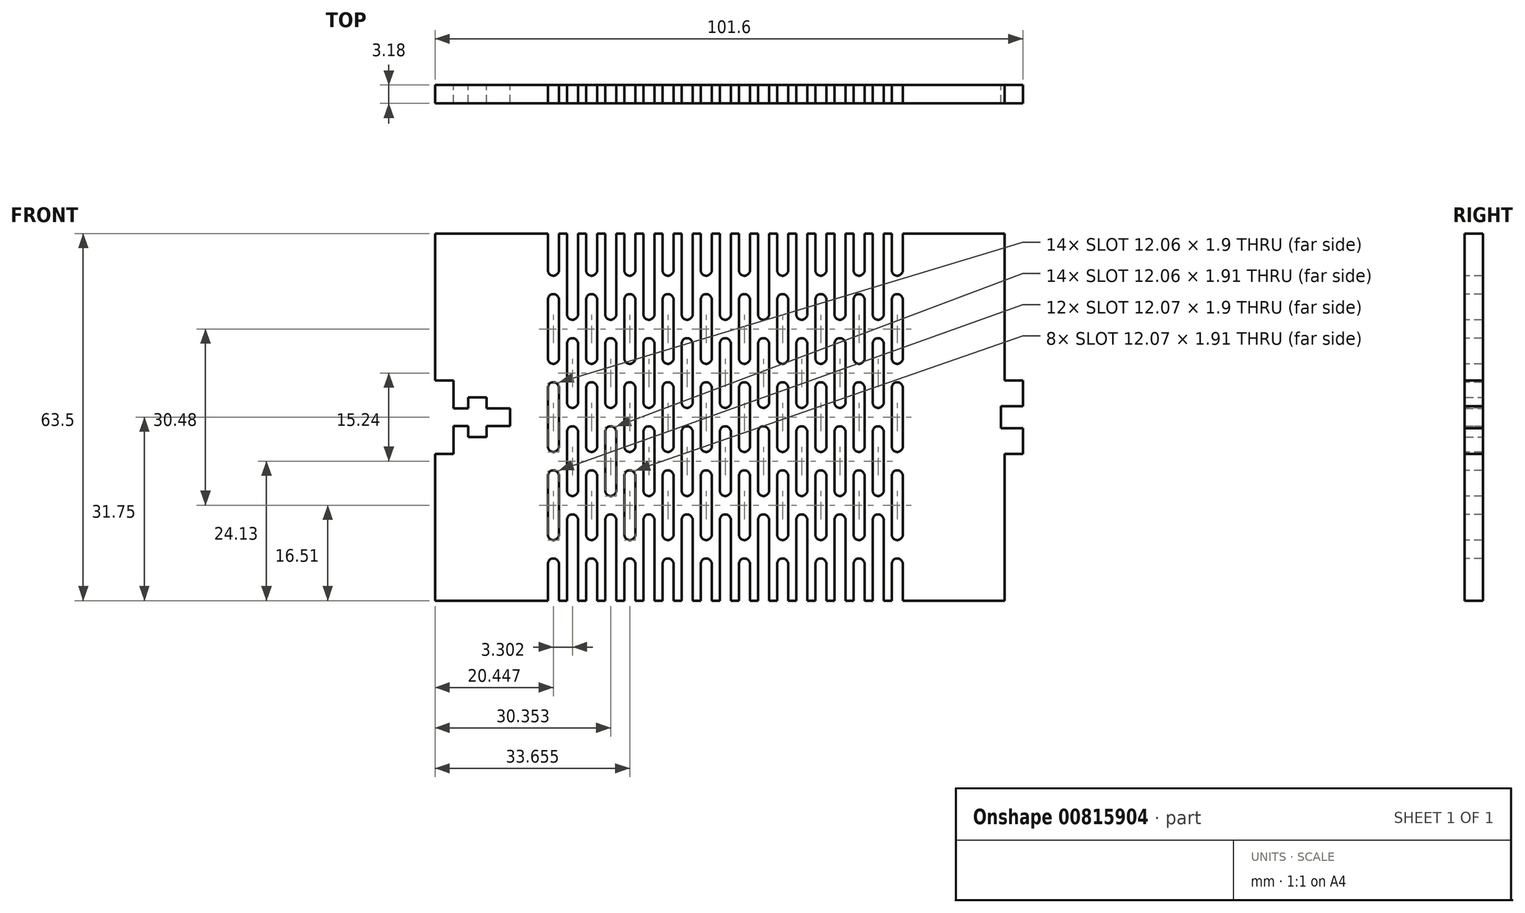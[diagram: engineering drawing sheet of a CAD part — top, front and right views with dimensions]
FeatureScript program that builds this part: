
annotation { "Feature Type Name" : "Feature", "Feature Type Description" : "" }
export const myFeature = defineFeature(function(context is Context, id is Id, definition is map)
    precondition{}
    {
        {
            var Q0;
            Q0=qCreatedBy(makeId("Front.planeOp"),FACE);
            var sketch = newSketch(context, id + "F0", { "sketchPlane" : qUnion([Q0])});
            skLineSegment(sketch, "E0.bottom", {"start": v(50.8, 31.75) * mm, "end": v(-50.8, 31.75) * mm});
            skLineSegment(sketch, "E0.top", {"start": v(50.8, -31.75) * mm, "end": v(-50.8, -31.75) * mm});
            skLineSegment(sketch, "E0.left", {"start": v(50.8, 31.75) * mm, "end": v(50.8, -31.75) * mm});
            skLineSegment(sketch, "E0.right", {"start": v(-50.8, 31.75) * mm, "end": v(-50.8, -31.75) * mm});
            skPoint(sketch, "E0.middle", {"position": v(0, 0) * mm});
            skLineSegment(sketch, "E1", {"start": v(-50.8, 0) * mm, "end": v(50.8, 0) * mm, "construction": true});
            skSolve(sketch);
        }
        {
            var Q0;
            Q0=makeQuery(id+"F0.imprint","IMPRINT",FACE,{"disambiguationData":[TD([[makeQuery(id+"F0.imprint","IMPRINT",EDGE,{"derivedFrom":sQuery(id+"F0.wireOp",EDGE,"E0.bottom")}),1.0]])]});
            extrude(context, id + "F1", {"entities" : qUnion([Q0]), "depth" : 3.17 * mm, "offsetDistance" : 25.4 * mm});
        }
        {
            var Q0;
            Q0=qCreatedBy(makeId("Front.planeOp"),FACE);
            var sketch = newSketch(context, id + "F2", { "sketchPlane" : qUnion([Q0])});
            skLineSegment(sketch, "E2", {"start": v(0, 0) * mm, "end": v(-50.8, 0) * mm, "construction": true});
            skLineSegment(sketch, "E3", {"start": v(0, 0) * mm, "end": v(50.8, 0) * mm, "construction": true});
            skLineSegment(sketch, "E4", {"start": v(50.8, 0) * mm, "end": v(50.8, 31.75) * mm, "construction": true});
            skLineSegment(sketch, "E5", {"start": v(50.8, 31.75) * mm, "end": v(47.63, 31.75) * mm});
            skLineSegment(sketch, "E6", {"start": v(47.63, 31.75) * mm, "end": v(47.63, 6.35) * mm});
            skLineSegment(sketch, "E7", {"start": v(47.63, 6.35) * mm, "end": v(50.8, 6.35) * mm});
            skLineSegment(sketch, "E8", {"start": v(50.8, 6.35) * mm, "end": v(50.8, 31.75) * mm});
            skLineSegment(sketch, "E9", {"start": v(50.8, 0) * mm, "end": v(50.8, 1.9) * mm});
            skLineSegment(sketch, "E10", {"start": v(50.8, 1.9) * mm, "end": v(47, 1.9) * mm});
            skLineSegment(sketch, "E11", {"start": v(47, 1.9) * mm, "end": v(47, 0) * mm});
            skLineSegment(sketch, "E12.MirrorCS", {"start": v(50.8, -6.35) * mm, "end": v(50.8, -31.75) * mm});
            skLineSegment(sketch, "E13.MirrorCS", {"start": v(50.8, 0) * mm, "end": v(50.8, -1.9) * mm});
            skLineSegment(sketch, "E14.MirrorCS", {"start": v(47.63, -31.75) * mm, "end": v(47.63, -6.35) * mm});
            skLineSegment(sketch, "E15.MirrorCS", {"start": v(50.8, -1.9) * mm, "end": v(47, -1.9) * mm});
            skLineSegment(sketch, "E16.MirrorCS", {"start": v(47.63, -6.35) * mm, "end": v(50.8, -6.35) * mm});
            skLineSegment(sketch, "E17.MirrorCS", {"start": v(50.8, 0) * mm, "end": v(50.8, -31.75) * mm, "construction": true});
            skLineSegment(sketch, "E18.MirrorCS", {"start": v(47, -1.9) * mm, "end": v(47, 0) * mm});
            skLineSegment(sketch, "E19.MirrorCS", {"start": v(50.8, -31.75) * mm, "end": v(47.63, -31.75) * mm});
            skLineSegment(sketch, "E20", {"start": v(-50.8, 0) * mm, "end": v(-50.8, -6.35) * mm});
            skLineSegment(sketch, "E21", {"start": v(-50.8, -6.35) * mm, "end": v(-47.63, -6.35) * mm});
            skLineSegment(sketch, "E22", {"start": v(-47.63, -6.35) * mm, "end": v(-47.63, -1.52) * mm});
            skLineSegment(sketch, "E23", {"start": v(-47.63, -1.52) * mm, "end": v(-45.09, -1.52) * mm});
            skLineSegment(sketch, "E24", {"start": v(-45.09, -1.52) * mm, "end": v(-45.09, -3.43) * mm});
            skLineSegment(sketch, "E25", {"start": v(-45.09, -3.43) * mm, "end": v(-41.91, -3.43) * mm});
            skLineSegment(sketch, "E26", {"start": v(-41.91, -3.43) * mm, "end": v(-41.91, -1.52) * mm});
            skLineSegment(sketch, "E27", {"start": v(-41.91, -1.52) * mm, "end": v(-37.85, -1.52) * mm});
            skLineSegment(sketch, "E28", {"start": v(-37.85, -1.52) * mm, "end": v(-37.85, 0) * mm});
            skLineSegment(sketch, "E29.MirrorCS", {"start": v(-50.8, 6.35) * mm, "end": v(-47.63, 6.35) * mm});
            skLineSegment(sketch, "E30.MirrorCS", {"start": v(-45.09, 1.52) * mm, "end": v(-45.09, 3.43) * mm});
            skLineSegment(sketch, "E31.MirrorCS", {"start": v(-45.09, 3.43) * mm, "end": v(-41.91, 3.43) * mm});
            skLineSegment(sketch, "E32.MirrorCS", {"start": v(-50.8, 0) * mm, "end": v(-50.8, 6.35) * mm});
            skLineSegment(sketch, "E33.MirrorCS", {"start": v(-41.91, 3.43) * mm, "end": v(-41.91, 1.52) * mm});
            skLineSegment(sketch, "E34.MirrorCS", {"start": v(-47.63, 1.52) * mm, "end": v(-45.09, 1.52) * mm});
            skLineSegment(sketch, "E35.MirrorCS", {"start": v(-47.63, 6.35) * mm, "end": v(-47.63, 1.52) * mm});
            skLineSegment(sketch, "E36.MirrorCS", {"start": v(-37.85, 1.52) * mm, "end": v(-37.85, 0) * mm});
            skLineSegment(sketch, "E37.MirrorCS", {"start": v(-41.91, 1.52) * mm, "end": v(-37.85, 1.52) * mm});
            skSolve(sketch);
        }
        {
            var Q0;
            Q0 = qSketchRegion(id + "F2", true);
            extrude(context, id + "F3", {"entities" : qUnion([Q0]), "operationType" : NewBodyOperationType.REMOVE, "depth" : 25.4 * mm, "offsetDistance" : 25.4 * mm});
        }
        {
            var Q0;
            Q0=makeQuery(id+"F1.opExtrude","CAP_FACE",FACE,{"disambiguationData":[OSD([sQuery(id+"F0.wireOp",EDGE,"E0.bottom"),sQuery(id+"F0.wireOp",EDGE,"E0.top"),sQuery(id+"F0.wireOp",EDGE,"E0.left"),sQuery(id+"F0.wireOp",EDGE,"E0.right")])],"isStart":false});
            var sketch = newSketch(context, id + "F4", { "sketchPlane" : qUnion([Q0])});
            skLineSegment(sketch, "E38", {"start": v(25.4, 31.75) * mm, "end": v(25.4, -31.75) * mm, "construction": true});
            skLineSegment(sketch, "E39", {"start": v(-25.4, 31.75) * mm, "end": v(-23.75, 31.75) * mm, "construction": true});
            skLineSegment(sketch, "E40", {"start": v(-23.75, 31.75) * mm, "end": v(-23.75, 25.4) * mm});
            skLineSegment(sketch, "E41", {"start": v(0, 0) * mm, "end": v(-25.4, 0) * mm, "construction": true});
            skLineSegment(sketch, "E42", {"start": v(-25.4, 0) * mm, "end": v(-25.4, 31.75) * mm, "construction": true});
            skLineSegment(sketch, "E43", {"start": v(-23.75, 25.4) * mm, "end": v(-23.75, 20.32) * mm, "construction": true});
            skLineSegment(sketch, "E44", {"start": v(-23.75, 20.32) * mm, "end": v(-23.75, 10.16) * mm});
            skLineSegment(sketch, "E45", {"start": v(-23.75, 10.16) * mm, "end": v(-23.75, 5.08) * mm, "construction": true});
            skLineSegment(sketch, "E46", {"start": v(-23.75, 5.08) * mm, "end": v(-23.75, 0) * mm});
            skArc(sketch, "E47.0.endCap", {"start": v(-22.8, 25.4) * mm, "mid": v(-23.75, 24.45) * mm, "end": v(-24.7, 25.4) * mm});
            skLineSegment(sketch, "E47.0.left", {"start": v(-22.8, 31.75) * mm, "end": v(-22.8, 25.4) * mm});
            skLineSegment(sketch, "E47.0.right", {"start": v(-24.7, 31.75) * mm, "end": v(-24.7, 25.4) * mm});
            skArc(sketch, "E48.0.startCap", {"start": v(-24.7, 20.32) * mm, "mid": v(-23.75, 21.27) * mm, "end": v(-22.8, 20.32) * mm});
            skArc(sketch, "E48.0.endCap", {"start": v(-22.8, 10.16) * mm, "mid": v(-23.75, 9.2) * mm, "end": v(-24.7, 10.16) * mm});
            skLineSegment(sketch, "E48.0.left", {"start": v(-22.8, 20.32) * mm, "end": v(-22.8, 10.16) * mm});
            skLineSegment(sketch, "E48.0.right", {"start": v(-24.7, 20.32) * mm, "end": v(-24.7, 10.16) * mm});
            skArc(sketch, "E49.0.startCap", {"start": v(-24.7, 5.08) * mm, "mid": v(-23.75, 6.03) * mm, "end": v(-22.8, 5.08) * mm});
            skLineSegment(sketch, "E49.0.left", {"start": v(-22.8, 5.08) * mm, "end": v(-22.8, 0) * mm});
            skLineSegment(sketch, "E49.0.right", {"start": v(-24.7, 5.08) * mm, "end": v(-24.7, 0) * mm});
            skLineSegment(sketch, "E50", {"start": v(-22.8, 31.75) * mm, "end": v(-24.7, 31.75) * mm});
            skLineSegment(sketch, "E51.MirrorCS", {"start": v(-25.4, -31.75) * mm, "end": v(-23.75, -31.75) * mm, "construction": true});
            skLineSegment(sketch, "E52.MirrorCS", {"start": v(-22.8, -31.75) * mm, "end": v(-24.7, -31.75) * mm});
            skArc(sketch, "E53.MirrorCS", {"start": v(-22.8, -10.16) * mm, "mid": v(-23.75, -9.2) * mm, "end": v(-24.7, -10.16) * mm});
            skLineSegment(sketch, "E54.MirrorCS", {"start": v(-24.7, -20.32) * mm, "end": v(-24.7, -10.16) * mm});
            skLineSegment(sketch, "E55.MirrorCS", {"start": v(-22.8, -20.32) * mm, "end": v(-22.8, -10.16) * mm});
            skLineSegment(sketch, "E56.MirrorCS", {"start": v(-23.75, -10.16) * mm, "end": v(-23.75, -5.08) * mm, "construction": true});
            skArc(sketch, "E57.MirrorCS", {"start": v(-22.8, -25.4) * mm, "mid": v(-23.75, -24.45) * mm, "end": v(-24.7, -25.4) * mm});
            skLineSegment(sketch, "E58.MirrorCS", {"start": v(-24.7, -31.75) * mm, "end": v(-24.7, -25.4) * mm});
            skLineSegment(sketch, "E59.MirrorCS", {"start": v(-25.4, 0) * mm, "end": v(-25.4, -31.75) * mm, "construction": true});
            skLineSegment(sketch, "E60.MirrorCS", {"start": v(-23.75, -25.4) * mm, "end": v(-23.75, -20.32) * mm, "construction": true});
            skLineSegment(sketch, "E61.MirrorCS", {"start": v(-22.8, -5.08) * mm, "end": v(-22.8, 0) * mm});
            skArc(sketch, "E62.MirrorCS", {"start": v(-24.7, -20.32) * mm, "mid": v(-23.75, -21.27) * mm, "end": v(-22.8, -20.32) * mm});
            skLineSegment(sketch, "E63.MirrorCS", {"start": v(-23.75, -31.75) * mm, "end": v(-23.75, -25.4) * mm});
            skLineSegment(sketch, "E64.MirrorCS", {"start": v(-23.75, -5.08) * mm, "end": v(-23.75, 0) * mm});
            skArc(sketch, "E65.MirrorCS", {"start": v(-24.7, -5.08) * mm, "mid": v(-23.75, -6.03) * mm, "end": v(-22.8, -5.08) * mm});
            skLineSegment(sketch, "E66.MirrorCS", {"start": v(-24.7, -5.08) * mm, "end": v(-24.7, 0) * mm});
            skLineSegment(sketch, "E67.MirrorCS", {"start": v(-23.75, -20.32) * mm, "end": v(-23.75, -10.16) * mm});
            skLineSegment(sketch, "E68.MirrorCS", {"start": v(-22.8, -31.75) * mm, "end": v(-22.8, -25.4) * mm});
            skLineSegment(sketch, "E69", {"start": v(-23.75, 31.75) * mm, "end": v(-20.45, 31.75) * mm, "construction": true});
            skLineSegment(sketch, "E70", {"start": v(-20.45, 31.75) * mm, "end": v(-20.45, 17.78) * mm});
            skLineSegment(sketch, "E71", {"start": v(-20.45, 17.78) * mm, "end": v(-20.45, 12.7) * mm, "construction": true});
            skLineSegment(sketch, "E72", {"start": v(-20.45, 12.7) * mm, "end": v(-20.45, 2.54) * mm});
            skLineSegment(sketch, "E73", {"start": v(-20.45, 2.54) * mm, "end": v(-20.45, 0) * mm, "construction": true});
            skArc(sketch, "E74.0.endCap", {"start": v(-19.5, 17.78) * mm, "mid": v(-20.45, 16.83) * mm, "end": v(-21.4, 17.78) * mm});
            skLineSegment(sketch, "E74.0.left", {"start": v(-19.5, 31.75) * mm, "end": v(-19.5, 17.78) * mm});
            skLineSegment(sketch, "E74.0.right", {"start": v(-21.4, 31.75) * mm, "end": v(-21.4, 17.78) * mm});
            skArc(sketch, "E75.0.startCap", {"start": v(-21.4, 12.7) * mm, "mid": v(-20.45, 13.65) * mm, "end": v(-19.5, 12.7) * mm});
            skArc(sketch, "E75.0.endCap", {"start": v(-19.5, 2.54) * mm, "mid": v(-20.45, 1.59) * mm, "end": v(-21.4, 2.54) * mm});
            skLineSegment(sketch, "E75.0.left", {"start": v(-19.5, 12.7) * mm, "end": v(-19.5, 2.54) * mm});
            skLineSegment(sketch, "E75.0.right", {"start": v(-21.4, 12.7) * mm, "end": v(-21.4, 2.54) * mm});
            skLineSegment(sketch, "E76", {"start": v(-21.4, 31.75) * mm, "end": v(-19.5, 31.75) * mm});
            skLineSegment(sketch, "E77.MirrorCS", {"start": v(-21.4, -31.75) * mm, "end": v(-19.5, -31.75) * mm});
            skArc(sketch, "E78.MirrorCS", {"start": v(-19.5, -17.78) * mm, "mid": v(-20.45, -16.83) * mm, "end": v(-21.4, -17.78) * mm});
            skLineSegment(sketch, "E79.MirrorCS", {"start": v(-20.45, -12.7) * mm, "end": v(-20.45, -2.54) * mm});
            skArc(sketch, "E80.MirrorCS", {"start": v(-19.5, -2.54) * mm, "mid": v(-20.45, -1.59) * mm, "end": v(-21.4, -2.54) * mm});
            skLineSegment(sketch, "E81.MirrorCS", {"start": v(-19.5, -12.7) * mm, "end": v(-19.5, -2.54) * mm});
            skLineSegment(sketch, "E82.MirrorCS", {"start": v(-21.4, -12.7) * mm, "end": v(-21.4, -2.54) * mm});
            skLineSegment(sketch, "E83.MirrorCS", {"start": v(-20.45, -17.78) * mm, "end": v(-20.45, -12.7) * mm, "construction": true});
            skLineSegment(sketch, "E84.MirrorCS", {"start": v(-20.45, -31.75) * mm, "end": v(-20.45, -17.78) * mm});
            skLineSegment(sketch, "E85.MirrorCS", {"start": v(-23.75, -31.75) * mm, "end": v(-20.45, -31.75) * mm, "construction": true});
            skLineSegment(sketch, "E86.MirrorCS", {"start": v(-19.5, -31.75) * mm, "end": v(-19.5, -17.78) * mm});
            skLineSegment(sketch, "E87.MirrorCS", {"start": v(-20.45, -2.54) * mm, "end": v(-20.45, 0) * mm, "construction": true});
            skLineSegment(sketch, "E88.MirrorCS", {"start": v(-21.4, -31.75) * mm, "end": v(-21.4, -17.78) * mm});
            skArc(sketch, "E89.MirrorCS", {"start": v(-21.4, -12.7) * mm, "mid": v(-20.45, -13.65) * mm, "end": v(-19.5, -12.7) * mm});
            skArc(sketch, "E90.1.0.0", {"start": v(-16.2, -25.4) * mm, "mid": v(-17.15, -24.45) * mm, "end": v(-18.1, -25.4) * mm});
            skLineSegment(sketch, "E90.1.0.1", {"start": v(-14.8, -12.7) * mm, "end": v(-14.8, -2.54) * mm});
            skLineSegment(sketch, "E90.1.0.2", {"start": v(-18.1, -31.75) * mm, "end": v(-18.1, -25.4) * mm});
            skLineSegment(sketch, "E90.1.0.3", {"start": v(-13.84, 31.75) * mm, "end": v(-13.84, 17.78) * mm});
            skLineSegment(sketch, "E90.1.0.4", {"start": v(-18.1, -20.32) * mm, "end": v(-18.1, -10.16) * mm});
            skArc(sketch, "E90.1.0.5", {"start": v(-18.1, 5.08) * mm, "mid": v(-17.15, 6.03) * mm, "end": v(-16.2, 5.08) * mm});
            skLineSegment(sketch, "E90.1.0.6", {"start": v(-17.15, 5.08) * mm, "end": v(-17.15, 0) * mm});
            skLineSegment(sketch, "E90.1.0.7", {"start": v(-12.9, 31.75) * mm, "end": v(-12.9, 17.78) * mm});
            skLineSegment(sketch, "E90.1.0.8", {"start": v(-14.8, 12.7) * mm, "end": v(-14.8, 2.54) * mm});
            skLineSegment(sketch, "E90.1.0.9", {"start": v(-13.84, -17.78) * mm, "end": v(-13.84, -12.7) * mm, "construction": true});
            skLineSegment(sketch, "E90.1.0.10", {"start": v(-13.84, 12.7) * mm, "end": v(-13.84, 2.54) * mm});
            skLineSegment(sketch, "E90.1.0.11", {"start": v(-17.15, -10.16) * mm, "end": v(-17.15, -5.08) * mm, "construction": true});
            skLineSegment(sketch, "E90.1.0.12", {"start": v(-17.15, -5.08) * mm, "end": v(-17.15, 0) * mm});
            skLineSegment(sketch, "E90.1.0.13", {"start": v(-13.84, 17.78) * mm, "end": v(-13.84, 12.7) * mm, "construction": true});
            skLineSegment(sketch, "E90.1.0.14", {"start": v(-16.2, 5.08) * mm, "end": v(-16.2, 0) * mm});
            skLineSegment(sketch, "E90.1.0.15", {"start": v(-18.1, 5.08) * mm, "end": v(-18.1, 0) * mm});
            skLineSegment(sketch, "E90.1.0.16", {"start": v(-12.9, -12.7) * mm, "end": v(-12.9, -2.54) * mm});
            skLineSegment(sketch, "E90.1.0.17", {"start": v(-16.2, -20.32) * mm, "end": v(-16.2, -10.16) * mm});
            skLineSegment(sketch, "E90.1.0.18", {"start": v(-16.2, 31.75) * mm, "end": v(-16.2, 25.4) * mm});
            skLineSegment(sketch, "E90.1.0.19", {"start": v(-13.84, -31.75) * mm, "end": v(-13.84, -17.78) * mm});
            skLineSegment(sketch, "E90.1.0.20", {"start": v(-17.15, -25.4) * mm, "end": v(-17.15, -20.32) * mm, "construction": true});
            skLineSegment(sketch, "E90.1.0.21", {"start": v(-14.8, 31.75) * mm, "end": v(-14.8, 17.78) * mm});
            skLineSegment(sketch, "E90.1.0.22", {"start": v(-16.2, -5.08) * mm, "end": v(-16.2, 0) * mm});
            skLineSegment(sketch, "E90.1.0.23", {"start": v(-17.15, -31.75) * mm, "end": v(-17.15, -25.4) * mm});
            skLineSegment(sketch, "E90.1.0.24", {"start": v(-13.84, -12.7) * mm, "end": v(-13.84, -2.54) * mm});
            skLineSegment(sketch, "E90.1.0.25", {"start": v(-12.9, 12.7) * mm, "end": v(-12.9, 2.54) * mm});
            skLineSegment(sketch, "E90.1.0.26", {"start": v(-17.15, 20.32) * mm, "end": v(-17.15, 10.16) * mm});
            skLineSegment(sketch, "E90.1.0.27", {"start": v(-12.9, -31.75) * mm, "end": v(-12.9, -17.78) * mm});
            skLineSegment(sketch, "E90.1.0.28", {"start": v(-17.15, -20.32) * mm, "end": v(-17.15, -10.16) * mm});
            skLineSegment(sketch, "E90.1.0.29", {"start": v(-16.2, 20.32) * mm, "end": v(-16.2, 10.16) * mm});
            skLineSegment(sketch, "E90.1.0.30", {"start": v(-17.15, 25.4) * mm, "end": v(-17.15, 20.32) * mm, "construction": true});
            skLineSegment(sketch, "E90.1.0.31", {"start": v(-17.15, 10.16) * mm, "end": v(-17.15, 5.08) * mm, "construction": true});
            skLineSegment(sketch, "E90.1.0.32", {"start": v(-16.2, -31.75) * mm, "end": v(-16.2, -25.4) * mm});
            skLineSegment(sketch, "E90.1.0.33", {"start": v(-18.1, -5.08) * mm, "end": v(-18.1, 0) * mm});
            skLineSegment(sketch, "E90.1.0.34", {"start": v(-18.1, 20.32) * mm, "end": v(-18.1, 10.16) * mm});
            skLineSegment(sketch, "E90.1.0.35", {"start": v(-14.8, -31.75) * mm, "end": v(-14.8, -17.78) * mm});
            skLineSegment(sketch, "E90.1.0.36", {"start": v(-17.15, 31.75) * mm, "end": v(-17.15, 25.4) * mm});
            skLineSegment(sketch, "E90.1.0.37", {"start": v(-18.1, 31.75) * mm, "end": v(-18.1, 25.4) * mm});
            skLineSegment(sketch, "E90.1.0.38", {"start": v(-13.84, -2.54) * mm, "end": v(-13.84, 0) * mm, "construction": true});
            skLineSegment(sketch, "E90.1.0.39", {"start": v(-14.8, 31.75) * mm, "end": v(-12.9, 31.75) * mm});
            skArc(sketch, "E90.1.0.40", {"start": v(-18.1, -5.08) * mm, "mid": v(-17.15, -6.03) * mm, "end": v(-16.2, -5.08) * mm});
            skLineSegment(sketch, "E90.1.0.41", {"start": v(-13.84, 2.54) * mm, "end": v(-13.84, 0) * mm, "construction": true});
            skArc(sketch, "E90.1.0.42", {"start": v(-16.2, 25.4) * mm, "mid": v(-17.15, 24.45) * mm, "end": v(-18.1, 25.4) * mm});
            skLineSegment(sketch, "E90.1.0.43", {"start": v(-14.8, -31.75) * mm, "end": v(-12.9, -31.75) * mm});
            skArc(sketch, "E90.1.0.44", {"start": v(-12.9, -2.54) * mm, "mid": v(-13.84, -1.59) * mm, "end": v(-14.8, -2.54) * mm});
            skArc(sketch, "E90.1.0.45", {"start": v(-12.9, -17.78) * mm, "mid": v(-13.84, -16.83) * mm, "end": v(-14.8, -17.78) * mm});
            skArc(sketch, "E90.1.0.46", {"start": v(-18.1, -20.32) * mm, "mid": v(-17.15, -21.27) * mm, "end": v(-16.2, -20.32) * mm});
            skArc(sketch, "E90.1.0.47", {"start": v(-12.9, 17.78) * mm, "mid": v(-13.84, 16.83) * mm, "end": v(-14.8, 17.78) * mm});
            skArc(sketch, "E90.1.0.48", {"start": v(-16.2, 10.16) * mm, "mid": v(-17.15, 9.2) * mm, "end": v(-18.1, 10.16) * mm});
            skArc(sketch, "E90.1.0.49", {"start": v(-18.1, 20.32) * mm, "mid": v(-17.15, 21.27) * mm, "end": v(-16.2, 20.32) * mm});
            skArc(sketch, "E90.1.0.50", {"start": v(-12.9, 2.54) * mm, "mid": v(-13.84, 1.59) * mm, "end": v(-14.8, 2.54) * mm});
            skArc(sketch, "E90.1.0.51", {"start": v(-16.2, -10.16) * mm, "mid": v(-17.15, -9.2) * mm, "end": v(-18.1, -10.16) * mm});
            skLineSegment(sketch, "E90.1.0.52", {"start": v(-16.2, -31.75) * mm, "end": v(-18.1, -31.75) * mm});
            skArc(sketch, "E90.1.0.53", {"start": v(-14.8, 12.7) * mm, "mid": v(-13.84, 13.65) * mm, "end": v(-12.9, 12.7) * mm});
            skLineSegment(sketch, "E90.1.0.54", {"start": v(-16.2, 31.75) * mm, "end": v(-18.1, 31.75) * mm});
            skArc(sketch, "E90.1.0.55", {"start": v(-14.8, -12.7) * mm, "mid": v(-13.84, -13.65) * mm, "end": v(-12.9, -12.7) * mm});
            skArc(sketch, "E90.2.0.0", {"start": v(-9.59, -25.4) * mm, "mid": v(-10.54, -24.45) * mm, "end": v(-11.5, -25.4) * mm});
            skLineSegment(sketch, "E90.2.0.1", {"start": v(-8.2, -12.7) * mm, "end": v(-8.2, -2.54) * mm});
            skLineSegment(sketch, "E90.2.0.2", {"start": v(-11.5, -31.75) * mm, "end": v(-11.5, -25.4) * mm});
            skLineSegment(sketch, "E90.2.0.3", {"start": v(-7.24, 31.75) * mm, "end": v(-7.24, 17.78) * mm});
            skLineSegment(sketch, "E90.2.0.4", {"start": v(-11.5, -20.32) * mm, "end": v(-11.5, -10.16) * mm});
            skArc(sketch, "E90.2.0.5", {"start": v(-11.5, 5.08) * mm, "mid": v(-10.54, 6.03) * mm, "end": v(-9.59, 5.08) * mm});
            skLineSegment(sketch, "E90.2.0.6", {"start": v(-10.54, 5.08) * mm, "end": v(-10.54, 0) * mm});
            skLineSegment(sketch, "E90.2.0.7", {"start": v(-6.29, 31.75) * mm, "end": v(-6.29, 17.78) * mm});
            skLineSegment(sketch, "E90.2.0.8", {"start": v(-8.2, 12.7) * mm, "end": v(-8.2, 2.54) * mm});
            skLineSegment(sketch, "E90.2.0.9", {"start": v(-7.24, -17.78) * mm, "end": v(-7.24, -12.7) * mm, "construction": true});
            skLineSegment(sketch, "E90.2.0.10", {"start": v(-7.24, 12.7) * mm, "end": v(-7.24, 2.54) * mm});
            skLineSegment(sketch, "E90.2.0.11", {"start": v(-10.54, -10.16) * mm, "end": v(-10.54, -5.08) * mm, "construction": true});
            skLineSegment(sketch, "E90.2.0.12", {"start": v(-10.54, -5.08) * mm, "end": v(-10.54, 0) * mm});
            skLineSegment(sketch, "E90.2.0.13", {"start": v(-7.24, 17.78) * mm, "end": v(-7.24, 12.7) * mm, "construction": true});
            skLineSegment(sketch, "E90.2.0.14", {"start": v(-9.59, 5.08) * mm, "end": v(-9.59, 0) * mm});
            skLineSegment(sketch, "E90.2.0.15", {"start": v(-11.5, 5.08) * mm, "end": v(-11.5, 0) * mm});
            skLineSegment(sketch, "E90.2.0.16", {"start": v(-6.29, -12.7) * mm, "end": v(-6.29, -2.54) * mm});
            skLineSegment(sketch, "E90.2.0.17", {"start": v(-9.59, -20.32) * mm, "end": v(-9.59, -10.16) * mm});
            skLineSegment(sketch, "E90.2.0.18", {"start": v(-9.59, 31.75) * mm, "end": v(-9.59, 25.4) * mm});
            skLineSegment(sketch, "E90.2.0.19", {"start": v(-7.24, -31.75) * mm, "end": v(-7.24, -17.78) * mm});
            skLineSegment(sketch, "E90.2.0.20", {"start": v(-10.54, -25.4) * mm, "end": v(-10.54, -20.32) * mm, "construction": true});
            skLineSegment(sketch, "E90.2.0.21", {"start": v(-8.2, 31.75) * mm, "end": v(-8.2, 17.78) * mm});
            skLineSegment(sketch, "E90.2.0.22", {"start": v(-9.59, -5.08) * mm, "end": v(-9.59, 0) * mm});
            skLineSegment(sketch, "E90.2.0.23", {"start": v(-10.54, -31.75) * mm, "end": v(-10.54, -25.4) * mm});
            skLineSegment(sketch, "E90.2.0.24", {"start": v(-7.24, -12.7) * mm, "end": v(-7.24, -2.54) * mm});
            skLineSegment(sketch, "E90.2.0.25", {"start": v(-6.29, 12.7) * mm, "end": v(-6.29, 2.54) * mm});
            skLineSegment(sketch, "E90.2.0.26", {"start": v(-10.54, 20.32) * mm, "end": v(-10.54, 10.16) * mm});
            skLineSegment(sketch, "E90.2.0.27", {"start": v(-6.29, -31.75) * mm, "end": v(-6.29, -17.78) * mm});
            skLineSegment(sketch, "E90.2.0.28", {"start": v(-10.54, -20.32) * mm, "end": v(-10.54, -10.16) * mm});
            skLineSegment(sketch, "E90.2.0.29", {"start": v(-9.59, 20.32) * mm, "end": v(-9.59, 10.16) * mm});
            skLineSegment(sketch, "E90.2.0.30", {"start": v(-10.54, 25.4) * mm, "end": v(-10.54, 20.32) * mm, "construction": true});
            skLineSegment(sketch, "E90.2.0.31", {"start": v(-10.54, 10.16) * mm, "end": v(-10.54, 5.08) * mm, "construction": true});
            skLineSegment(sketch, "E90.2.0.32", {"start": v(-9.59, -31.75) * mm, "end": v(-9.59, -25.4) * mm});
            skLineSegment(sketch, "E90.2.0.33", {"start": v(-11.5, -5.08) * mm, "end": v(-11.5, 0) * mm});
            skLineSegment(sketch, "E90.2.0.34", {"start": v(-11.5, 20.32) * mm, "end": v(-11.5, 10.16) * mm});
            skLineSegment(sketch, "E90.2.0.35", {"start": v(-8.2, -31.75) * mm, "end": v(-8.2, -17.78) * mm});
            skLineSegment(sketch, "E90.2.0.36", {"start": v(-10.54, 31.75) * mm, "end": v(-10.54, 25.4) * mm});
            skLineSegment(sketch, "E90.2.0.37", {"start": v(-11.5, 31.75) * mm, "end": v(-11.5, 25.4) * mm});
            skLineSegment(sketch, "E90.2.0.38", {"start": v(-7.24, -2.54) * mm, "end": v(-7.24, 0) * mm, "construction": true});
            skLineSegment(sketch, "E90.2.0.39", {"start": v(-8.2, 31.75) * mm, "end": v(-6.29, 31.75) * mm});
            skArc(sketch, "E90.2.0.40", {"start": v(-11.5, -5.08) * mm, "mid": v(-10.54, -6.03) * mm, "end": v(-9.59, -5.08) * mm});
            skLineSegment(sketch, "E90.2.0.41", {"start": v(-7.24, 2.54) * mm, "end": v(-7.24, 0) * mm, "construction": true});
            skArc(sketch, "E90.2.0.42", {"start": v(-9.59, 25.4) * mm, "mid": v(-10.54, 24.45) * mm, "end": v(-11.5, 25.4) * mm});
            skLineSegment(sketch, "E90.2.0.43", {"start": v(-8.2, -31.75) * mm, "end": v(-6.29, -31.75) * mm});
            skArc(sketch, "E90.2.0.44", {"start": v(-6.29, -2.54) * mm, "mid": v(-7.24, -1.59) * mm, "end": v(-8.2, -2.54) * mm});
            skArc(sketch, "E90.2.0.45", {"start": v(-6.29, -17.78) * mm, "mid": v(-7.24, -16.83) * mm, "end": v(-8.2, -17.78) * mm});
            skArc(sketch, "E90.2.0.46", {"start": v(-11.5, -20.32) * mm, "mid": v(-10.54, -21.27) * mm, "end": v(-9.59, -20.32) * mm});
            skArc(sketch, "E90.2.0.47", {"start": v(-6.29, 17.78) * mm, "mid": v(-7.24, 16.83) * mm, "end": v(-8.2, 17.78) * mm});
            skArc(sketch, "E90.2.0.48", {"start": v(-9.59, 10.16) * mm, "mid": v(-10.54, 9.2) * mm, "end": v(-11.5, 10.16) * mm});
            skArc(sketch, "E90.2.0.49", {"start": v(-11.5, 20.32) * mm, "mid": v(-10.54, 21.27) * mm, "end": v(-9.59, 20.32) * mm});
            skArc(sketch, "E90.2.0.50", {"start": v(-6.29, 2.54) * mm, "mid": v(-7.24, 1.59) * mm, "end": v(-8.2, 2.54) * mm});
            skArc(sketch, "E90.2.0.51", {"start": v(-9.59, -10.16) * mm, "mid": v(-10.54, -9.2) * mm, "end": v(-11.5, -10.16) * mm});
            skLineSegment(sketch, "E90.2.0.52", {"start": v(-9.59, -31.75) * mm, "end": v(-11.5, -31.75) * mm});
            skArc(sketch, "E90.2.0.53", {"start": v(-8.2, 12.7) * mm, "mid": v(-7.24, 13.65) * mm, "end": v(-6.29, 12.7) * mm});
            skLineSegment(sketch, "E90.2.0.54", {"start": v(-9.59, 31.75) * mm, "end": v(-11.5, 31.75) * mm});
            skArc(sketch, "E90.2.0.55", {"start": v(-8.2, -12.7) * mm, "mid": v(-7.24, -13.65) * mm, "end": v(-6.29, -12.7) * mm});
            skArc(sketch, "E90.3.0.0", {"start": v(-2.98, -25.4) * mm, "mid": v(-3.94, -24.45) * mm, "end": v(-4.89, -25.4) * mm});
            skLineSegment(sketch, "E90.3.0.1", {"start": v(-1.59, -12.7) * mm, "end": v(-1.59, -2.54) * mm});
            skLineSegment(sketch, "E90.3.0.2", {"start": v(-4.89, -31.75) * mm, "end": v(-4.89, -25.4) * mm});
            skLineSegment(sketch, "E90.3.0.3", {"start": v(-0.64, 31.75) * mm, "end": v(-0.64, 17.78) * mm});
            skLineSegment(sketch, "E90.3.0.4", {"start": v(-4.89, -20.32) * mm, "end": v(-4.89, -10.16) * mm});
            skArc(sketch, "E90.3.0.5", {"start": v(-4.89, 5.08) * mm, "mid": v(-3.94, 6.03) * mm, "end": v(-2.98, 5.08) * mm});
            skLineSegment(sketch, "E90.3.0.6", {"start": v(-3.94, 5.08) * mm, "end": v(-3.94, 0) * mm});
            skLineSegment(sketch, "E90.3.0.7", {"start": v(0.32, 31.75) * mm, "end": v(0.32, 17.78) * mm});
            skLineSegment(sketch, "E90.3.0.8", {"start": v(-1.59, 12.7) * mm, "end": v(-1.59, 2.54) * mm});
            skLineSegment(sketch, "E90.3.0.9", {"start": v(-0.64, -17.78) * mm, "end": v(-0.64, -12.7) * mm, "construction": true});
            skLineSegment(sketch, "E90.3.0.10", {"start": v(-0.64, 12.7) * mm, "end": v(-0.64, 2.54) * mm});
            skLineSegment(sketch, "E90.3.0.11", {"start": v(-3.94, -10.16) * mm, "end": v(-3.94, -5.08) * mm, "construction": true});
            skLineSegment(sketch, "E90.3.0.12", {"start": v(-3.94, -5.08) * mm, "end": v(-3.94, 0) * mm});
            skLineSegment(sketch, "E90.3.0.13", {"start": v(-0.64, 17.78) * mm, "end": v(-0.64, 12.7) * mm, "construction": true});
            skLineSegment(sketch, "E90.3.0.14", {"start": v(-2.98, 5.08) * mm, "end": v(-2.98, 0) * mm});
            skLineSegment(sketch, "E90.3.0.15", {"start": v(-4.89, 5.08) * mm, "end": v(-4.89, 0) * mm});
            skLineSegment(sketch, "E90.3.0.16", {"start": v(0.32, -12.7) * mm, "end": v(0.32, -2.54) * mm});
            skLineSegment(sketch, "E90.3.0.17", {"start": v(-2.98, -20.32) * mm, "end": v(-2.98, -10.16) * mm});
            skLineSegment(sketch, "E90.3.0.18", {"start": v(-2.98, 31.75) * mm, "end": v(-2.98, 25.4) * mm});
            skLineSegment(sketch, "E90.3.0.19", {"start": v(-0.64, -31.75) * mm, "end": v(-0.64, -17.78) * mm});
            skLineSegment(sketch, "E90.3.0.20", {"start": v(-3.94, -25.4) * mm, "end": v(-3.94, -20.32) * mm, "construction": true});
            skLineSegment(sketch, "E90.3.0.21", {"start": v(-1.59, 31.75) * mm, "end": v(-1.59, 17.78) * mm});
            skLineSegment(sketch, "E90.3.0.22", {"start": v(-2.98, -5.08) * mm, "end": v(-2.98, 0) * mm});
            skLineSegment(sketch, "E90.3.0.23", {"start": v(-3.94, -31.75) * mm, "end": v(-3.94, -25.4) * mm});
            skLineSegment(sketch, "E90.3.0.24", {"start": v(-0.64, -12.7) * mm, "end": v(-0.64, -2.54) * mm});
            skLineSegment(sketch, "E90.3.0.25", {"start": v(0.32, 12.7) * mm, "end": v(0.32, 2.54) * mm});
            skLineSegment(sketch, "E90.3.0.26", {"start": v(-3.94, 20.32) * mm, "end": v(-3.94, 10.16) * mm});
            skLineSegment(sketch, "E90.3.0.27", {"start": v(0.32, -31.75) * mm, "end": v(0.32, -17.78) * mm});
            skLineSegment(sketch, "E90.3.0.28", {"start": v(-3.94, -20.32) * mm, "end": v(-3.94, -10.16) * mm});
            skLineSegment(sketch, "E90.3.0.29", {"start": v(-2.98, 20.32) * mm, "end": v(-2.98, 10.16) * mm});
            skLineSegment(sketch, "E90.3.0.30", {"start": v(-3.94, 25.4) * mm, "end": v(-3.94, 20.32) * mm, "construction": true});
            skLineSegment(sketch, "E90.3.0.31", {"start": v(-3.94, 10.16) * mm, "end": v(-3.94, 5.08) * mm, "construction": true});
            skLineSegment(sketch, "E90.3.0.32", {"start": v(-2.98, -31.75) * mm, "end": v(-2.98, -25.4) * mm});
            skLineSegment(sketch, "E90.3.0.33", {"start": v(-4.89, -5.08) * mm, "end": v(-4.89, 0) * mm});
            skLineSegment(sketch, "E90.3.0.34", {"start": v(-4.89, 20.32) * mm, "end": v(-4.89, 10.16) * mm});
            skLineSegment(sketch, "E90.3.0.35", {"start": v(-1.59, -31.75) * mm, "end": v(-1.59, -17.78) * mm});
            skLineSegment(sketch, "E90.3.0.36", {"start": v(-3.94, 31.75) * mm, "end": v(-3.94, 25.4) * mm});
            skLineSegment(sketch, "E90.3.0.37", {"start": v(-4.89, 31.75) * mm, "end": v(-4.89, 25.4) * mm});
            skLineSegment(sketch, "E90.3.0.38", {"start": v(-0.64, -2.54) * mm, "end": v(-0.64, 0) * mm, "construction": true});
            skLineSegment(sketch, "E90.3.0.39", {"start": v(-1.59, 31.75) * mm, "end": v(0.32, 31.75) * mm});
            skArc(sketch, "E90.3.0.40", {"start": v(-4.89, -5.08) * mm, "mid": v(-3.94, -6.03) * mm, "end": v(-2.98, -5.08) * mm});
            skLineSegment(sketch, "E90.3.0.41", {"start": v(-0.64, 2.54) * mm, "end": v(-0.64, 0) * mm, "construction": true});
            skArc(sketch, "E90.3.0.42", {"start": v(-2.98, 25.4) * mm, "mid": v(-3.94, 24.45) * mm, "end": v(-4.89, 25.4) * mm});
            skLineSegment(sketch, "E90.3.0.43", {"start": v(-1.59, -31.75) * mm, "end": v(0.32, -31.75) * mm});
            skArc(sketch, "E90.3.0.44", {"start": v(0.32, -2.54) * mm, "mid": v(-0.64, -1.59) * mm, "end": v(-1.59, -2.54) * mm});
            skArc(sketch, "E90.3.0.45", {"start": v(0.32, -17.78) * mm, "mid": v(-0.64, -16.83) * mm, "end": v(-1.59, -17.78) * mm});
            skArc(sketch, "E90.3.0.46", {"start": v(-4.89, -20.32) * mm, "mid": v(-3.94, -21.27) * mm, "end": v(-2.98, -20.32) * mm});
            skArc(sketch, "E90.3.0.47", {"start": v(0.32, 17.78) * mm, "mid": v(-0.64, 16.83) * mm, "end": v(-1.59, 17.78) * mm});
            skArc(sketch, "E90.3.0.48", {"start": v(-2.98, 10.16) * mm, "mid": v(-3.94, 9.2) * mm, "end": v(-4.89, 10.16) * mm});
            skArc(sketch, "E90.3.0.49", {"start": v(-4.89, 20.32) * mm, "mid": v(-3.94, 21.27) * mm, "end": v(-2.98, 20.32) * mm});
            skArc(sketch, "E90.3.0.50", {"start": v(0.32, 2.54) * mm, "mid": v(-0.64, 1.59) * mm, "end": v(-1.59, 2.54) * mm});
            skArc(sketch, "E90.3.0.51", {"start": v(-2.98, -10.16) * mm, "mid": v(-3.94, -9.2) * mm, "end": v(-4.89, -10.16) * mm});
            skLineSegment(sketch, "E90.3.0.52", {"start": v(-2.98, -31.75) * mm, "end": v(-4.89, -31.75) * mm});
            skArc(sketch, "E90.3.0.53", {"start": v(-1.59, 12.7) * mm, "mid": v(-0.64, 13.65) * mm, "end": v(0.32, 12.7) * mm});
            skLineSegment(sketch, "E90.3.0.54", {"start": v(-2.98, 31.75) * mm, "end": v(-4.89, 31.75) * mm});
            skArc(sketch, "E90.3.0.55", {"start": v(-1.59, -12.7) * mm, "mid": v(-0.64, -13.65) * mm, "end": v(0.32, -12.7) * mm});
            skArc(sketch, "E90.4.0.0", {"start": v(3.62, -25.4) * mm, "mid": v(2.67, -24.45) * mm, "end": v(1.71, -25.4) * mm});
            skLineSegment(sketch, "E90.4.0.1", {"start": v(5.02, -12.7) * mm, "end": v(5.02, -2.54) * mm});
            skLineSegment(sketch, "E90.4.0.2", {"start": v(1.71, -31.75) * mm, "end": v(1.71, -25.4) * mm});
            skLineSegment(sketch, "E90.4.0.3", {"start": v(5.97, 31.75) * mm, "end": v(5.97, 17.78) * mm});
            skLineSegment(sketch, "E90.4.0.4", {"start": v(1.71, -20.32) * mm, "end": v(1.71, -10.16) * mm});
            skArc(sketch, "E90.4.0.5", {"start": v(1.71, 5.08) * mm, "mid": v(2.67, 6.03) * mm, "end": v(3.62, 5.08) * mm});
            skLineSegment(sketch, "E90.4.0.6", {"start": v(2.67, 5.08) * mm, "end": v(2.67, 0) * mm});
            skLineSegment(sketch, "E90.4.0.7", {"start": v(6.92, 31.75) * mm, "end": v(6.92, 17.78) * mm});
            skLineSegment(sketch, "E90.4.0.8", {"start": v(5.02, 12.7) * mm, "end": v(5.02, 2.54) * mm});
            skLineSegment(sketch, "E90.4.0.9", {"start": v(5.97, -17.78) * mm, "end": v(5.97, -12.7) * mm, "construction": true});
            skLineSegment(sketch, "E90.4.0.10", {"start": v(5.97, 12.7) * mm, "end": v(5.97, 2.54) * mm});
            skLineSegment(sketch, "E90.4.0.11", {"start": v(2.67, -10.16) * mm, "end": v(2.67, -5.08) * mm, "construction": true});
            skLineSegment(sketch, "E90.4.0.12", {"start": v(2.67, -5.08) * mm, "end": v(2.67, 0) * mm});
            skLineSegment(sketch, "E90.4.0.13", {"start": v(5.97, 17.78) * mm, "end": v(5.97, 12.7) * mm, "construction": true});
            skLineSegment(sketch, "E90.4.0.14", {"start": v(3.62, 5.08) * mm, "end": v(3.62, 0) * mm});
            skLineSegment(sketch, "E90.4.0.15", {"start": v(1.71, 5.08) * mm, "end": v(1.71, 0) * mm});
            skLineSegment(sketch, "E90.4.0.16", {"start": v(6.92, -12.7) * mm, "end": v(6.92, -2.54) * mm});
            skLineSegment(sketch, "E90.4.0.17", {"start": v(3.62, -20.32) * mm, "end": v(3.62, -10.16) * mm});
            skLineSegment(sketch, "E90.4.0.18", {"start": v(3.62, 31.75) * mm, "end": v(3.62, 25.4) * mm});
            skLineSegment(sketch, "E90.4.0.19", {"start": v(5.97, -31.75) * mm, "end": v(5.97, -17.78) * mm});
            skLineSegment(sketch, "E90.4.0.20", {"start": v(2.67, -25.4) * mm, "end": v(2.67, -20.32) * mm, "construction": true});
            skLineSegment(sketch, "E90.4.0.21", {"start": v(5.02, 31.75) * mm, "end": v(5.02, 17.78) * mm});
            skLineSegment(sketch, "E90.4.0.22", {"start": v(3.62, -5.08) * mm, "end": v(3.62, 0) * mm});
            skLineSegment(sketch, "E90.4.0.23", {"start": v(2.67, -31.75) * mm, "end": v(2.67, -25.4) * mm});
            skLineSegment(sketch, "E90.4.0.24", {"start": v(5.97, -12.7) * mm, "end": v(5.97, -2.54) * mm});
            skLineSegment(sketch, "E90.4.0.25", {"start": v(6.92, 12.7) * mm, "end": v(6.92, 2.54) * mm});
            skLineSegment(sketch, "E90.4.0.26", {"start": v(2.67, 20.32) * mm, "end": v(2.67, 10.16) * mm});
            skLineSegment(sketch, "E90.4.0.27", {"start": v(6.92, -31.75) * mm, "end": v(6.92, -17.78) * mm});
            skLineSegment(sketch, "E90.4.0.28", {"start": v(2.67, -20.32) * mm, "end": v(2.67, -10.16) * mm});
            skLineSegment(sketch, "E90.4.0.29", {"start": v(3.62, 20.32) * mm, "end": v(3.62, 10.16) * mm});
            skLineSegment(sketch, "E90.4.0.30", {"start": v(2.67, 25.4) * mm, "end": v(2.67, 20.32) * mm, "construction": true});
            skLineSegment(sketch, "E90.4.0.31", {"start": v(2.67, 10.16) * mm, "end": v(2.67, 5.08) * mm, "construction": true});
            skLineSegment(sketch, "E90.4.0.32", {"start": v(3.62, -31.75) * mm, "end": v(3.62, -25.4) * mm});
            skLineSegment(sketch, "E90.4.0.33", {"start": v(1.71, -5.08) * mm, "end": v(1.71, 0) * mm});
            skLineSegment(sketch, "E90.4.0.34", {"start": v(1.71, 20.32) * mm, "end": v(1.71, 10.16) * mm});
            skLineSegment(sketch, "E90.4.0.35", {"start": v(5.02, -31.75) * mm, "end": v(5.02, -17.78) * mm});
            skLineSegment(sketch, "E90.4.0.36", {"start": v(2.67, 31.75) * mm, "end": v(2.67, 25.4) * mm});
            skLineSegment(sketch, "E90.4.0.37", {"start": v(1.71, 31.75) * mm, "end": v(1.71, 25.4) * mm});
            skLineSegment(sketch, "E90.4.0.38", {"start": v(5.97, -2.54) * mm, "end": v(5.97, 0) * mm, "construction": true});
            skLineSegment(sketch, "E90.4.0.39", {"start": v(5.02, 31.75) * mm, "end": v(6.92, 31.75) * mm});
            skArc(sketch, "E90.4.0.40", {"start": v(1.71, -5.08) * mm, "mid": v(2.67, -6.03) * mm, "end": v(3.62, -5.08) * mm});
            skLineSegment(sketch, "E90.4.0.41", {"start": v(5.97, 2.54) * mm, "end": v(5.97, 0) * mm, "construction": true});
            skArc(sketch, "E90.4.0.42", {"start": v(3.62, 25.4) * mm, "mid": v(2.67, 24.45) * mm, "end": v(1.71, 25.4) * mm});
            skLineSegment(sketch, "E90.4.0.43", {"start": v(5.02, -31.75) * mm, "end": v(6.92, -31.75) * mm});
            skArc(sketch, "E90.4.0.44", {"start": v(6.92, -2.54) * mm, "mid": v(5.97, -1.59) * mm, "end": v(5.02, -2.54) * mm});
            skArc(sketch, "E90.4.0.45", {"start": v(6.92, -17.78) * mm, "mid": v(5.97, -16.83) * mm, "end": v(5.02, -17.78) * mm});
            skArc(sketch, "E90.4.0.46", {"start": v(1.71, -20.32) * mm, "mid": v(2.67, -21.27) * mm, "end": v(3.62, -20.32) * mm});
            skArc(sketch, "E90.4.0.47", {"start": v(6.92, 17.78) * mm, "mid": v(5.97, 16.83) * mm, "end": v(5.02, 17.78) * mm});
            skArc(sketch, "E90.4.0.48", {"start": v(3.62, 10.16) * mm, "mid": v(2.67, 9.2) * mm, "end": v(1.71, 10.16) * mm});
            skArc(sketch, "E90.4.0.49", {"start": v(1.71, 20.32) * mm, "mid": v(2.67, 21.27) * mm, "end": v(3.62, 20.32) * mm});
            skArc(sketch, "E90.4.0.50", {"start": v(6.92, 2.54) * mm, "mid": v(5.97, 1.59) * mm, "end": v(5.02, 2.54) * mm});
            skArc(sketch, "E90.4.0.51", {"start": v(3.62, -10.16) * mm, "mid": v(2.67, -9.2) * mm, "end": v(1.71, -10.16) * mm});
            skLineSegment(sketch, "E90.4.0.52", {"start": v(3.62, -31.75) * mm, "end": v(1.71, -31.75) * mm});
            skArc(sketch, "E90.4.0.53", {"start": v(5.02, 12.7) * mm, "mid": v(5.97, 13.65) * mm, "end": v(6.92, 12.7) * mm});
            skLineSegment(sketch, "E90.4.0.54", {"start": v(3.62, 31.75) * mm, "end": v(1.71, 31.75) * mm});
            skArc(sketch, "E90.4.0.55", {"start": v(5.02, -12.7) * mm, "mid": v(5.97, -13.65) * mm, "end": v(6.92, -12.7) * mm});
            skArc(sketch, "E90.5.0.0", {"start": v(10.22, -25.4) * mm, "mid": v(9.27, -24.45) * mm, "end": v(8.32, -25.4) * mm});
            skLineSegment(sketch, "E90.5.0.1", {"start": v(11.62, -12.7) * mm, "end": v(11.62, -2.54) * mm});
            skLineSegment(sketch, "E90.5.0.2", {"start": v(8.32, -31.75) * mm, "end": v(8.32, -25.4) * mm});
            skLineSegment(sketch, "E90.5.0.3", {"start": v(12.57, 31.75) * mm, "end": v(12.57, 17.78) * mm});
            skLineSegment(sketch, "E90.5.0.4", {"start": v(8.32, -20.32) * mm, "end": v(8.32, -10.16) * mm});
            skArc(sketch, "E90.5.0.5", {"start": v(8.32, 5.08) * mm, "mid": v(9.27, 6.03) * mm, "end": v(10.22, 5.08) * mm});
            skLineSegment(sketch, "E90.5.0.6", {"start": v(9.27, 5.08) * mm, "end": v(9.27, 0) * mm});
            skLineSegment(sketch, "E90.5.0.7", {"start": v(13.53, 31.75) * mm, "end": v(13.53, 17.78) * mm});
            skLineSegment(sketch, "E90.5.0.8", {"start": v(11.62, 12.7) * mm, "end": v(11.62, 2.54) * mm});
            skLineSegment(sketch, "E90.5.0.9", {"start": v(12.57, -17.78) * mm, "end": v(12.57, -12.7) * mm, "construction": true});
            skLineSegment(sketch, "E90.5.0.10", {"start": v(12.57, 12.7) * mm, "end": v(12.57, 2.54) * mm});
            skLineSegment(sketch, "E90.5.0.11", {"start": v(9.27, -10.16) * mm, "end": v(9.27, -5.08) * mm, "construction": true});
            skLineSegment(sketch, "E90.5.0.12", {"start": v(9.27, -5.08) * mm, "end": v(9.27, 0) * mm});
            skLineSegment(sketch, "E90.5.0.13", {"start": v(12.57, 17.78) * mm, "end": v(12.57, 12.7) * mm, "construction": true});
            skLineSegment(sketch, "E90.5.0.14", {"start": v(10.22, 5.08) * mm, "end": v(10.22, 0) * mm});
            skLineSegment(sketch, "E90.5.0.15", {"start": v(8.32, 5.08) * mm, "end": v(8.32, 0) * mm});
            skLineSegment(sketch, "E90.5.0.16", {"start": v(13.53, -12.7) * mm, "end": v(13.53, -2.54) * mm});
            skLineSegment(sketch, "E90.5.0.17", {"start": v(10.22, -20.32) * mm, "end": v(10.22, -10.16) * mm});
            skLineSegment(sketch, "E90.5.0.18", {"start": v(10.22, 31.75) * mm, "end": v(10.22, 25.4) * mm});
            skLineSegment(sketch, "E90.5.0.19", {"start": v(12.57, -31.75) * mm, "end": v(12.57, -17.78) * mm});
            skLineSegment(sketch, "E90.5.0.20", {"start": v(9.27, -25.4) * mm, "end": v(9.27, -20.32) * mm, "construction": true});
            skLineSegment(sketch, "E90.5.0.21", {"start": v(11.62, 31.75) * mm, "end": v(11.62, 17.78) * mm});
            skLineSegment(sketch, "E90.5.0.22", {"start": v(10.22, -5.08) * mm, "end": v(10.22, 0) * mm});
            skLineSegment(sketch, "E90.5.0.23", {"start": v(9.27, -31.75) * mm, "end": v(9.27, -25.4) * mm});
            skLineSegment(sketch, "E90.5.0.24", {"start": v(12.57, -12.7) * mm, "end": v(12.57, -2.54) * mm});
            skLineSegment(sketch, "E90.5.0.25", {"start": v(13.53, 12.7) * mm, "end": v(13.53, 2.54) * mm});
            skLineSegment(sketch, "E90.5.0.26", {"start": v(9.27, 20.32) * mm, "end": v(9.27, 10.16) * mm});
            skLineSegment(sketch, "E90.5.0.27", {"start": v(13.53, -31.75) * mm, "end": v(13.53, -17.78) * mm});
            skLineSegment(sketch, "E90.5.0.28", {"start": v(9.27, -20.32) * mm, "end": v(9.27, -10.16) * mm});
            skLineSegment(sketch, "E90.5.0.29", {"start": v(10.22, 20.32) * mm, "end": v(10.22, 10.16) * mm});
            skLineSegment(sketch, "E90.5.0.30", {"start": v(9.27, 25.4) * mm, "end": v(9.27, 20.32) * mm, "construction": true});
            skLineSegment(sketch, "E90.5.0.31", {"start": v(9.27, 10.16) * mm, "end": v(9.27, 5.08) * mm, "construction": true});
            skLineSegment(sketch, "E90.5.0.32", {"start": v(10.22, -31.75) * mm, "end": v(10.22, -25.4) * mm});
            skLineSegment(sketch, "E90.5.0.33", {"start": v(8.32, -5.08) * mm, "end": v(8.32, 0) * mm});
            skLineSegment(sketch, "E90.5.0.34", {"start": v(8.32, 20.32) * mm, "end": v(8.32, 10.16) * mm});
            skLineSegment(sketch, "E90.5.0.35", {"start": v(11.62, -31.75) * mm, "end": v(11.62, -17.78) * mm});
            skLineSegment(sketch, "E90.5.0.36", {"start": v(9.27, 31.75) * mm, "end": v(9.27, 25.4) * mm});
            skLineSegment(sketch, "E90.5.0.37", {"start": v(8.32, 31.75) * mm, "end": v(8.32, 25.4) * mm});
            skLineSegment(sketch, "E90.5.0.38", {"start": v(12.57, -2.54) * mm, "end": v(12.57, 0) * mm, "construction": true});
            skLineSegment(sketch, "E90.5.0.39", {"start": v(11.62, 31.75) * mm, "end": v(13.53, 31.75) * mm});
            skArc(sketch, "E90.5.0.40", {"start": v(8.32, -5.08) * mm, "mid": v(9.27, -6.03) * mm, "end": v(10.22, -5.08) * mm});
            skLineSegment(sketch, "E90.5.0.41", {"start": v(12.57, 2.54) * mm, "end": v(12.57, 0) * mm, "construction": true});
            skArc(sketch, "E90.5.0.42", {"start": v(10.22, 25.4) * mm, "mid": v(9.27, 24.45) * mm, "end": v(8.32, 25.4) * mm});
            skLineSegment(sketch, "E90.5.0.43", {"start": v(11.62, -31.75) * mm, "end": v(13.53, -31.75) * mm});
            skArc(sketch, "E90.5.0.44", {"start": v(13.53, -2.54) * mm, "mid": v(12.57, -1.59) * mm, "end": v(11.62, -2.54) * mm});
            skArc(sketch, "E90.5.0.45", {"start": v(13.53, -17.78) * mm, "mid": v(12.57, -16.83) * mm, "end": v(11.62, -17.78) * mm});
            skArc(sketch, "E90.5.0.46", {"start": v(8.32, -20.32) * mm, "mid": v(9.27, -21.27) * mm, "end": v(10.22, -20.32) * mm});
            skArc(sketch, "E90.5.0.47", {"start": v(13.53, 17.78) * mm, "mid": v(12.57, 16.83) * mm, "end": v(11.62, 17.78) * mm});
            skArc(sketch, "E90.5.0.48", {"start": v(10.22, 10.16) * mm, "mid": v(9.27, 9.2) * mm, "end": v(8.32, 10.16) * mm});
            skArc(sketch, "E90.5.0.49", {"start": v(8.32, 20.32) * mm, "mid": v(9.27, 21.27) * mm, "end": v(10.22, 20.32) * mm});
            skArc(sketch, "E90.5.0.50", {"start": v(13.53, 2.54) * mm, "mid": v(12.57, 1.59) * mm, "end": v(11.62, 2.54) * mm});
            skArc(sketch, "E90.5.0.51", {"start": v(10.22, -10.16) * mm, "mid": v(9.27, -9.2) * mm, "end": v(8.32, -10.16) * mm});
            skLineSegment(sketch, "E90.5.0.52", {"start": v(10.22, -31.75) * mm, "end": v(8.32, -31.75) * mm});
            skArc(sketch, "E90.5.0.53", {"start": v(11.62, 12.7) * mm, "mid": v(12.57, 13.65) * mm, "end": v(13.53, 12.7) * mm});
            skLineSegment(sketch, "E90.5.0.54", {"start": v(10.22, 31.75) * mm, "end": v(8.32, 31.75) * mm});
            skArc(sketch, "E90.5.0.55", {"start": v(11.62, -12.7) * mm, "mid": v(12.57, -13.65) * mm, "end": v(13.53, -12.7) * mm});
            skArc(sketch, "E90.6.0.0", {"start": v(16.83, -25.4) * mm, "mid": v(15.87, -24.45) * mm, "end": v(14.92, -25.4) * mm});
            skLineSegment(sketch, "E90.6.0.1", {"start": v(18.22, -12.7) * mm, "end": v(18.22, -2.54) * mm});
            skLineSegment(sketch, "E90.6.0.2", {"start": v(14.92, -31.75) * mm, "end": v(14.92, -25.4) * mm});
            skLineSegment(sketch, "E90.6.0.3", {"start": v(19.18, 31.75) * mm, "end": v(19.18, 17.78) * mm});
            skLineSegment(sketch, "E90.6.0.4", {"start": v(14.92, -20.32) * mm, "end": v(14.92, -10.16) * mm});
            skArc(sketch, "E90.6.0.5", {"start": v(14.92, 5.08) * mm, "mid": v(15.87, 6.03) * mm, "end": v(16.83, 5.08) * mm});
            skLineSegment(sketch, "E90.6.0.6", {"start": v(15.87, 5.08) * mm, "end": v(15.87, 0) * mm});
            skLineSegment(sketch, "E90.6.0.7", {"start": v(20.13, 31.75) * mm, "end": v(20.13, 17.78) * mm});
            skLineSegment(sketch, "E90.6.0.8", {"start": v(18.22, 12.7) * mm, "end": v(18.22, 2.54) * mm});
            skLineSegment(sketch, "E90.6.0.9", {"start": v(19.18, -17.78) * mm, "end": v(19.18, -12.7) * mm, "construction": true});
            skLineSegment(sketch, "E90.6.0.10", {"start": v(19.18, 12.7) * mm, "end": v(19.18, 2.54) * mm});
            skLineSegment(sketch, "E90.6.0.11", {"start": v(15.87, -10.16) * mm, "end": v(15.87, -5.08) * mm, "construction": true});
            skLineSegment(sketch, "E90.6.0.12", {"start": v(15.87, -5.08) * mm, "end": v(15.87, 0) * mm});
            skLineSegment(sketch, "E90.6.0.13", {"start": v(19.18, 17.78) * mm, "end": v(19.18, 12.7) * mm, "construction": true});
            skLineSegment(sketch, "E90.6.0.14", {"start": v(16.83, 5.08) * mm, "end": v(16.83, 0) * mm});
            skLineSegment(sketch, "E90.6.0.15", {"start": v(14.92, 5.08) * mm, "end": v(14.92, 0) * mm});
            skLineSegment(sketch, "E90.6.0.16", {"start": v(20.13, -12.7) * mm, "end": v(20.13, -2.54) * mm});
            skLineSegment(sketch, "E90.6.0.17", {"start": v(16.83, -20.32) * mm, "end": v(16.83, -10.16) * mm});
            skLineSegment(sketch, "E90.6.0.18", {"start": v(16.83, 31.75) * mm, "end": v(16.83, 25.4) * mm});
            skLineSegment(sketch, "E90.6.0.19", {"start": v(19.18, -31.75) * mm, "end": v(19.18, -17.78) * mm});
            skLineSegment(sketch, "E90.6.0.20", {"start": v(15.87, -25.4) * mm, "end": v(15.87, -20.32) * mm, "construction": true});
            skLineSegment(sketch, "E90.6.0.21", {"start": v(18.22, 31.75) * mm, "end": v(18.22, 17.78) * mm});
            skLineSegment(sketch, "E90.6.0.22", {"start": v(16.83, -5.08) * mm, "end": v(16.83, 0) * mm});
            skLineSegment(sketch, "E90.6.0.23", {"start": v(15.87, -31.75) * mm, "end": v(15.87, -25.4) * mm});
            skLineSegment(sketch, "E90.6.0.24", {"start": v(19.18, -12.7) * mm, "end": v(19.18, -2.54) * mm});
            skLineSegment(sketch, "E90.6.0.25", {"start": v(20.13, 12.7) * mm, "end": v(20.13, 2.54) * mm});
            skLineSegment(sketch, "E90.6.0.26", {"start": v(15.87, 20.32) * mm, "end": v(15.87, 10.16) * mm});
            skLineSegment(sketch, "E90.6.0.27", {"start": v(20.13, -31.75) * mm, "end": v(20.13, -17.78) * mm});
            skLineSegment(sketch, "E90.6.0.28", {"start": v(15.87, -20.32) * mm, "end": v(15.87, -10.16) * mm});
            skLineSegment(sketch, "E90.6.0.29", {"start": v(16.83, 20.32) * mm, "end": v(16.83, 10.16) * mm});
            skLineSegment(sketch, "E90.6.0.30", {"start": v(15.87, 25.4) * mm, "end": v(15.87, 20.32) * mm, "construction": true});
            skLineSegment(sketch, "E90.6.0.31", {"start": v(15.87, 10.16) * mm, "end": v(15.87, 5.08) * mm, "construction": true});
            skLineSegment(sketch, "E90.6.0.32", {"start": v(16.83, -31.75) * mm, "end": v(16.83, -25.4) * mm});
            skLineSegment(sketch, "E90.6.0.33", {"start": v(14.92, -5.08) * mm, "end": v(14.92, 0) * mm});
            skLineSegment(sketch, "E90.6.0.34", {"start": v(14.92, 20.32) * mm, "end": v(14.92, 10.16) * mm});
            skLineSegment(sketch, "E90.6.0.35", {"start": v(18.22, -31.75) * mm, "end": v(18.22, -17.78) * mm});
            skLineSegment(sketch, "E90.6.0.36", {"start": v(15.87, 31.75) * mm, "end": v(15.87, 25.4) * mm});
            skLineSegment(sketch, "E90.6.0.37", {"start": v(14.92, 31.75) * mm, "end": v(14.92, 25.4) * mm});
            skLineSegment(sketch, "E90.6.0.38", {"start": v(19.18, -2.54) * mm, "end": v(19.18, 0) * mm, "construction": true});
            skLineSegment(sketch, "E90.6.0.39", {"start": v(18.22, 31.75) * mm, "end": v(20.13, 31.75) * mm});
            skArc(sketch, "E90.6.0.40", {"start": v(14.92, -5.08) * mm, "mid": v(15.87, -6.03) * mm, "end": v(16.83, -5.08) * mm});
            skLineSegment(sketch, "E90.6.0.41", {"start": v(19.18, 2.54) * mm, "end": v(19.18, 0) * mm, "construction": true});
            skArc(sketch, "E90.6.0.42", {"start": v(16.83, 25.4) * mm, "mid": v(15.87, 24.45) * mm, "end": v(14.92, 25.4) * mm});
            skLineSegment(sketch, "E90.6.0.43", {"start": v(18.22, -31.75) * mm, "end": v(20.13, -31.75) * mm});
            skArc(sketch, "E90.6.0.44", {"start": v(20.13, -2.54) * mm, "mid": v(19.18, -1.59) * mm, "end": v(18.22, -2.54) * mm});
            skArc(sketch, "E90.6.0.45", {"start": v(20.13, -17.78) * mm, "mid": v(19.18, -16.83) * mm, "end": v(18.22, -17.78) * mm});
            skArc(sketch, "E90.6.0.46", {"start": v(14.92, -20.32) * mm, "mid": v(15.87, -21.27) * mm, "end": v(16.83, -20.32) * mm});
            skArc(sketch, "E90.6.0.47", {"start": v(20.13, 17.78) * mm, "mid": v(19.18, 16.83) * mm, "end": v(18.22, 17.78) * mm});
            skArc(sketch, "E90.6.0.48", {"start": v(16.83, 10.16) * mm, "mid": v(15.87, 9.2) * mm, "end": v(14.92, 10.16) * mm});
            skArc(sketch, "E90.6.0.49", {"start": v(14.92, 20.32) * mm, "mid": v(15.87, 21.27) * mm, "end": v(16.83, 20.32) * mm});
            skArc(sketch, "E90.6.0.50", {"start": v(20.13, 2.54) * mm, "mid": v(19.18, 1.59) * mm, "end": v(18.22, 2.54) * mm});
            skArc(sketch, "E90.6.0.51", {"start": v(16.83, -10.16) * mm, "mid": v(15.87, -9.2) * mm, "end": v(14.92, -10.16) * mm});
            skLineSegment(sketch, "E90.6.0.52", {"start": v(16.83, -31.75) * mm, "end": v(14.92, -31.75) * mm});
            skArc(sketch, "E90.6.0.53", {"start": v(18.22, 12.7) * mm, "mid": v(19.18, 13.65) * mm, "end": v(20.13, 12.7) * mm});
            skLineSegment(sketch, "E90.6.0.54", {"start": v(16.83, 31.75) * mm, "end": v(14.92, 31.75) * mm});
            skArc(sketch, "E90.6.0.55", {"start": v(18.22, -12.7) * mm, "mid": v(19.18, -13.65) * mm, "end": v(20.13, -12.7) * mm});
            skArc(sketch, "E90.7.0.0", {"start": v(23.43, -25.4) * mm, "mid": v(22.48, -24.45) * mm, "end": v(21.53, -25.4) * mm});
            skLineSegment(sketch, "E90.7.0.1", {"start": v(24.83, -12.7) * mm, "end": v(24.83, -2.54) * mm});
            skLineSegment(sketch, "E90.7.0.2", {"start": v(21.53, -31.75) * mm, "end": v(21.53, -25.4) * mm});
            skLineSegment(sketch, "E90.7.0.3", {"start": v(25.78, 31.75) * mm, "end": v(25.78, 17.78) * mm});
            skLineSegment(sketch, "E90.7.0.4", {"start": v(21.53, -20.32) * mm, "end": v(21.53, -10.16) * mm});
            skArc(sketch, "E90.7.0.5", {"start": v(21.53, 5.08) * mm, "mid": v(22.48, 6.03) * mm, "end": v(23.43, 5.08) * mm});
            skLineSegment(sketch, "E90.7.0.6", {"start": v(22.48, 5.08) * mm, "end": v(22.48, 0) * mm});
            skLineSegment(sketch, "E90.7.0.7", {"start": v(26.73, 31.75) * mm, "end": v(26.73, 17.78) * mm});
            skLineSegment(sketch, "E90.7.0.8", {"start": v(24.83, 12.7) * mm, "end": v(24.83, 2.54) * mm});
            skLineSegment(sketch, "E90.7.0.9", {"start": v(25.78, -17.78) * mm, "end": v(25.78, -12.7) * mm, "construction": true});
            skLineSegment(sketch, "E90.7.0.10", {"start": v(25.78, 12.7) * mm, "end": v(25.78, 2.54) * mm});
            skLineSegment(sketch, "E90.7.0.11", {"start": v(22.48, -10.16) * mm, "end": v(22.48, -5.08) * mm, "construction": true});
            skLineSegment(sketch, "E90.7.0.12", {"start": v(22.48, -5.08) * mm, "end": v(22.48, 0) * mm});
            skLineSegment(sketch, "E90.7.0.13", {"start": v(25.78, 17.78) * mm, "end": v(25.78, 12.7) * mm, "construction": true});
            skLineSegment(sketch, "E90.7.0.14", {"start": v(23.43, 5.08) * mm, "end": v(23.43, 0) * mm});
            skLineSegment(sketch, "E90.7.0.15", {"start": v(21.53, 5.08) * mm, "end": v(21.53, 0) * mm});
            skLineSegment(sketch, "E90.7.0.16", {"start": v(26.73, -12.7) * mm, "end": v(26.73, -2.54) * mm});
            skLineSegment(sketch, "E90.7.0.17", {"start": v(23.43, -20.32) * mm, "end": v(23.43, -10.16) * mm});
            skLineSegment(sketch, "E90.7.0.18", {"start": v(23.43, 31.75) * mm, "end": v(23.43, 25.4) * mm});
            skLineSegment(sketch, "E90.7.0.19", {"start": v(25.78, -31.75) * mm, "end": v(25.78, -17.78) * mm});
            skLineSegment(sketch, "E90.7.0.20", {"start": v(22.48, -25.4) * mm, "end": v(22.48, -20.32) * mm, "construction": true});
            skLineSegment(sketch, "E90.7.0.21", {"start": v(24.83, 31.75) * mm, "end": v(24.83, 17.78) * mm});
            skLineSegment(sketch, "E90.7.0.22", {"start": v(23.43, -5.08) * mm, "end": v(23.43, 0) * mm});
            skLineSegment(sketch, "E90.7.0.23", {"start": v(22.48, -31.75) * mm, "end": v(22.48, -25.4) * mm});
            skLineSegment(sketch, "E90.7.0.24", {"start": v(25.78, -12.7) * mm, "end": v(25.78, -2.54) * mm});
            skLineSegment(sketch, "E90.7.0.25", {"start": v(26.73, 12.7) * mm, "end": v(26.73, 2.54) * mm});
            skLineSegment(sketch, "E90.7.0.26", {"start": v(22.48, 20.32) * mm, "end": v(22.48, 10.16) * mm});
            skLineSegment(sketch, "E90.7.0.27", {"start": v(26.73, -31.75) * mm, "end": v(26.73, -17.78) * mm});
            skLineSegment(sketch, "E90.7.0.28", {"start": v(22.48, -20.32) * mm, "end": v(22.48, -10.16) * mm});
            skLineSegment(sketch, "E90.7.0.29", {"start": v(23.43, 20.32) * mm, "end": v(23.43, 10.16) * mm});
            skLineSegment(sketch, "E90.7.0.30", {"start": v(22.48, 25.4) * mm, "end": v(22.48, 20.32) * mm, "construction": true});
            skLineSegment(sketch, "E90.7.0.31", {"start": v(22.48, 10.16) * mm, "end": v(22.48, 5.08) * mm, "construction": true});
            skLineSegment(sketch, "E90.7.0.32", {"start": v(23.43, -31.75) * mm, "end": v(23.43, -25.4) * mm});
            skLineSegment(sketch, "E90.7.0.33", {"start": v(21.53, -5.08) * mm, "end": v(21.53, 0) * mm});
            skLineSegment(sketch, "E90.7.0.34", {"start": v(21.53, 20.32) * mm, "end": v(21.53, 10.16) * mm});
            skLineSegment(sketch, "E90.7.0.35", {"start": v(24.83, -31.75) * mm, "end": v(24.83, -17.78) * mm});
            skLineSegment(sketch, "E90.7.0.36", {"start": v(22.48, 31.75) * mm, "end": v(22.48, 25.4) * mm});
            skLineSegment(sketch, "E90.7.0.37", {"start": v(21.53, 31.75) * mm, "end": v(21.53, 25.4) * mm});
            skLineSegment(sketch, "E90.7.0.38", {"start": v(25.78, -2.54) * mm, "end": v(25.78, 0) * mm, "construction": true});
            skLineSegment(sketch, "E90.7.0.39", {"start": v(24.83, 31.75) * mm, "end": v(26.73, 31.75) * mm});
            skArc(sketch, "E90.7.0.40", {"start": v(21.53, -5.08) * mm, "mid": v(22.48, -6.03) * mm, "end": v(23.43, -5.08) * mm});
            skLineSegment(sketch, "E90.7.0.41", {"start": v(25.78, 2.54) * mm, "end": v(25.78, 0) * mm, "construction": true});
            skArc(sketch, "E90.7.0.42", {"start": v(23.43, 25.4) * mm, "mid": v(22.48, 24.45) * mm, "end": v(21.53, 25.4) * mm});
            skLineSegment(sketch, "E90.7.0.43", {"start": v(24.83, -31.75) * mm, "end": v(26.73, -31.75) * mm});
            skArc(sketch, "E90.7.0.44", {"start": v(26.73, -2.54) * mm, "mid": v(25.78, -1.59) * mm, "end": v(24.83, -2.54) * mm});
            skArc(sketch, "E90.7.0.45", {"start": v(26.73, -17.78) * mm, "mid": v(25.78, -16.83) * mm, "end": v(24.83, -17.78) * mm});
            skArc(sketch, "E90.7.0.46", {"start": v(21.53, -20.32) * mm, "mid": v(22.48, -21.27) * mm, "end": v(23.43, -20.32) * mm});
            skArc(sketch, "E90.7.0.47", {"start": v(26.73, 17.78) * mm, "mid": v(25.78, 16.83) * mm, "end": v(24.83, 17.78) * mm});
            skArc(sketch, "E90.7.0.48", {"start": v(23.43, 10.16) * mm, "mid": v(22.48, 9.2) * mm, "end": v(21.53, 10.16) * mm});
            skArc(sketch, "E90.7.0.49", {"start": v(21.53, 20.32) * mm, "mid": v(22.48, 21.27) * mm, "end": v(23.43, 20.32) * mm});
            skArc(sketch, "E90.7.0.50", {"start": v(26.73, 2.54) * mm, "mid": v(25.78, 1.59) * mm, "end": v(24.83, 2.54) * mm});
            skArc(sketch, "E90.7.0.51", {"start": v(23.43, -10.16) * mm, "mid": v(22.48, -9.2) * mm, "end": v(21.53, -10.16) * mm});
            skLineSegment(sketch, "E90.7.0.52", {"start": v(23.43, -31.75) * mm, "end": v(21.53, -31.75) * mm});
            skArc(sketch, "E90.7.0.53", {"start": v(24.83, 12.7) * mm, "mid": v(25.78, 13.65) * mm, "end": v(26.73, 12.7) * mm});
            skLineSegment(sketch, "E90.7.0.54", {"start": v(23.43, 31.75) * mm, "end": v(21.53, 31.75) * mm});
            skArc(sketch, "E90.7.0.55", {"start": v(24.83, -12.7) * mm, "mid": v(25.78, -13.65) * mm, "end": v(26.73, -12.7) * mm});
            skLineSegment(sketch, "E90.direction1", {"start": v(-24.7, -31.75) * mm, "end": v(-18.1, -31.75) * mm, "construction": true});
            skLineSegment(sketch, "E91.1.0.0", {"start": v(-30.35, 10.16) * mm, "end": v(-30.35, 5.08) * mm, "construction": true});
            skLineSegment(sketch, "E91.1.0.1", {"start": v(-30.35, 20.32) * mm, "end": v(-30.35, 10.16) * mm});
            skLineSegment(sketch, "E91.1.0.2", {"start": v(-29.4, 20.32) * mm, "end": v(-29.4, 10.16) * mm});
            skLineSegment(sketch, "E91.1.0.3", {"start": v(-32, 0) * mm, "end": v(-32, 31.75) * mm, "construction": true});
            skLineSegment(sketch, "E91.1.0.4", {"start": v(-30.35, 25.4) * mm, "end": v(-30.35, 20.32) * mm, "construction": true});
            skLineSegment(sketch, "E91.1.0.5", {"start": v(-30.35, 31.75) * mm, "end": v(-30.35, 25.4) * mm});
            skLineSegment(sketch, "E91.1.0.6", {"start": v(-31.3, 20.32) * mm, "end": v(-31.3, 10.16) * mm});
            skLineSegment(sketch, "E91.1.0.7", {"start": v(-26.1, -31.75) * mm, "end": v(-26.1, -17.78) * mm});
            skLineSegment(sketch, "E91.1.0.8", {"start": v(-32, 0) * mm, "end": v(-32, -31.75) * mm, "construction": true});
            skLineSegment(sketch, "E91.1.0.9", {"start": v(-26.1, 31.75) * mm, "end": v(-26.1, 17.78) * mm});
            skLineSegment(sketch, "E91.1.0.10", {"start": v(-27.05, -12.7) * mm, "end": v(-27.05, -2.54) * mm});
            skLineSegment(sketch, "E91.1.0.11", {"start": v(-29.4, -31.75) * mm, "end": v(-29.4, -25.4) * mm});
            skLineSegment(sketch, "E91.1.0.12", {"start": v(-26.1, 12.7) * mm, "end": v(-26.1, 2.54) * mm});
            skLineSegment(sketch, "E91.1.0.13", {"start": v(-30.35, -10.16) * mm, "end": v(-30.35, -5.08) * mm, "construction": true});
            skLineSegment(sketch, "E91.1.0.14", {"start": v(-29.4, 5.08) * mm, "end": v(-29.4, 0) * mm});
            skLineSegment(sketch, "E91.1.0.15", {"start": v(-27.05, 12.7) * mm, "end": v(-27.05, 2.54) * mm});
            skLineSegment(sketch, "E91.1.0.16", {"start": v(-30.35, -20.32) * mm, "end": v(-30.35, -10.16) * mm});
            skLineSegment(sketch, "E91.1.0.17", {"start": v(-27.05, -17.78) * mm, "end": v(-27.05, -12.7) * mm, "construction": true});
            skLineSegment(sketch, "E91.1.0.18", {"start": v(-31.3, -20.32) * mm, "end": v(-31.3, -10.16) * mm});
            skLineSegment(sketch, "E91.1.0.19", {"start": v(-27.05, 31.75) * mm, "end": v(-27.05, 17.78) * mm});
            skLineSegment(sketch, "E91.1.0.20", {"start": v(-26.1, -12.7) * mm, "end": v(-26.1, -2.54) * mm});
            skLineSegment(sketch, "E91.1.0.21", {"start": v(-28, -12.7) * mm, "end": v(-28, -2.54) * mm});
            skLineSegment(sketch, "E91.1.0.22", {"start": v(-27.05, 17.78) * mm, "end": v(-27.05, 12.7) * mm, "construction": true});
            skLineSegment(sketch, "E91.1.0.23", {"start": v(-30.35, -25.4) * mm, "end": v(-30.35, -20.32) * mm, "construction": true});
            skLineSegment(sketch, "E91.1.0.24", {"start": v(-29.4, -20.32) * mm, "end": v(-29.4, -10.16) * mm});
            skLineSegment(sketch, "E91.1.0.25", {"start": v(-28, 31.75) * mm, "end": v(-28, 17.78) * mm});
            skLineSegment(sketch, "E91.1.0.26", {"start": v(-27.05, -31.75) * mm, "end": v(-27.05, -17.78) * mm});
            skLineSegment(sketch, "E91.1.0.27", {"start": v(-30.35, -5.08) * mm, "end": v(-30.35, 0) * mm});
            skLineSegment(sketch, "E91.1.0.28", {"start": v(-28, 12.7) * mm, "end": v(-28, 2.54) * mm});
            skLineSegment(sketch, "E91.1.0.29", {"start": v(-29.4, -5.08) * mm, "end": v(-29.4, 0) * mm});
            skLineSegment(sketch, "E91.1.0.30", {"start": v(-31.3, 5.08) * mm, "end": v(-31.3, 0) * mm});
            skLineSegment(sketch, "E91.1.0.31", {"start": v(-29.4, 31.75) * mm, "end": v(-29.4, 25.4) * mm});
            skLineSegment(sketch, "E91.1.0.32", {"start": v(-31.3, -31.75) * mm, "end": v(-31.3, -25.4) * mm});
            skLineSegment(sketch, "E91.1.0.33", {"start": v(-31.3, 31.75) * mm, "end": v(-31.3, 25.4) * mm});
            skLineSegment(sketch, "E91.1.0.34", {"start": v(-30.35, -31.75) * mm, "end": v(-30.35, -25.4) * mm});
            skLineSegment(sketch, "E91.1.0.35", {"start": v(-28, -31.75) * mm, "end": v(-28, -17.78) * mm});
            skLineSegment(sketch, "E91.1.0.36", {"start": v(-31.3, -5.08) * mm, "end": v(-31.3, 0) * mm});
            skLineSegment(sketch, "E91.1.0.37", {"start": v(-30.35, 5.08) * mm, "end": v(-30.35, 0) * mm});
            skArc(sketch, "E91.1.0.38", {"start": v(-28, -12.7) * mm, "mid": v(-27.05, -13.65) * mm, "end": v(-26.1, -12.7) * mm});
            skArc(sketch, "E91.1.0.39", {"start": v(-29.4, 25.4) * mm, "mid": v(-30.35, 24.45) * mm, "end": v(-31.3, 25.4) * mm});
            skArc(sketch, "E91.1.0.40", {"start": v(-31.3, 5.08) * mm, "mid": v(-30.35, 6.03) * mm, "end": v(-29.4, 5.08) * mm});
            skArc(sketch, "E91.1.0.41", {"start": v(-31.3, -20.32) * mm, "mid": v(-30.35, -21.27) * mm, "end": v(-29.4, -20.32) * mm});
            skLineSegment(sketch, "E91.1.0.42", {"start": v(-6.6, 0) * mm, "end": v(-32, 0) * mm, "construction": true});
            skArc(sketch, "E91.1.0.43", {"start": v(-29.4, 10.16) * mm, "mid": v(-30.35, 9.2) * mm, "end": v(-31.3, 10.16) * mm});
            skArc(sketch, "E91.1.0.44", {"start": v(-26.1, -2.54) * mm, "mid": v(-27.05, -1.59) * mm, "end": v(-28, -2.54) * mm});
            skLineSegment(sketch, "E91.1.0.45", {"start": v(-27.05, -2.54) * mm, "end": v(-27.05, 0) * mm, "construction": true});
            skArc(sketch, "E91.1.0.46", {"start": v(-29.4, -25.4) * mm, "mid": v(-30.35, -24.45) * mm, "end": v(-31.3, -25.4) * mm});
            skLineSegment(sketch, "E91.1.0.47", {"start": v(-27.05, 2.54) * mm, "end": v(-27.05, 0) * mm, "construction": true});
            skArc(sketch, "E91.1.0.48", {"start": v(-31.3, 20.32) * mm, "mid": v(-30.35, 21.27) * mm, "end": v(-29.4, 20.32) * mm});
            skLineSegment(sketch, "E91.1.0.49", {"start": v(-28, -31.75) * mm, "end": v(-26.1, -31.75) * mm});
            skLineSegment(sketch, "E91.1.0.50", {"start": v(-31.3, -31.75) * mm, "end": v(-24.7, -31.75) * mm, "construction": true});
            skLineSegment(sketch, "E91.1.0.51", {"start": v(-30.35, 31.75) * mm, "end": v(-27.05, 31.75) * mm, "construction": true});
            skLineSegment(sketch, "E91.1.0.52", {"start": v(-28, 31.75) * mm, "end": v(-26.1, 31.75) * mm});
            skLineSegment(sketch, "E91.1.0.53", {"start": v(-30.35, -31.75) * mm, "end": v(-27.05, -31.75) * mm, "construction": true});
            skArc(sketch, "E91.1.0.54", {"start": v(-26.1, 17.78) * mm, "mid": v(-27.05, 16.83) * mm, "end": v(-28, 17.78) * mm});
            skLineSegment(sketch, "E91.1.0.55", {"start": v(-29.4, -31.75) * mm, "end": v(-31.3, -31.75) * mm});
            skLineSegment(sketch, "E91.1.0.56", {"start": v(-32, 31.75) * mm, "end": v(-30.35, 31.75) * mm, "construction": true});
            skArc(sketch, "E91.1.0.57", {"start": v(-26.1, -17.78) * mm, "mid": v(-27.05, -16.83) * mm, "end": v(-28, -17.78) * mm});
            skLineSegment(sketch, "E91.1.0.58", {"start": v(-29.4, 31.75) * mm, "end": v(-31.3, 31.75) * mm});
            skArc(sketch, "E91.1.0.59", {"start": v(-29.4, -10.16) * mm, "mid": v(-30.35, -9.2) * mm, "end": v(-31.3, -10.16) * mm});
            skArc(sketch, "E91.1.0.60", {"start": v(-26.1, 2.54) * mm, "mid": v(-27.05, 1.59) * mm, "end": v(-28, 2.54) * mm});
            skArc(sketch, "E91.1.0.61", {"start": v(-31.3, -5.08) * mm, "mid": v(-30.35, -6.03) * mm, "end": v(-29.4, -5.08) * mm});
            skArc(sketch, "E91.1.0.62", {"start": v(-28, 12.7) * mm, "mid": v(-27.05, 13.65) * mm, "end": v(-26.1, 12.7) * mm});
            skLineSegment(sketch, "E91.1.0.63", {"start": v(-32, -31.75) * mm, "end": v(-30.35, -31.75) * mm, "construction": true});
            skLineSegment(sketch, "E91.direction1", {"start": v(-25.4, -31.75) * mm, "end": v(-32, -31.75) * mm, "construction": true});
            skArc(sketch, "E92.0.8.0", {"start": v(30.04, -25.4) * mm, "mid": v(29.08, -24.45) * mm, "end": v(28.13, -25.4) * mm});
            skLineSegment(sketch, "E92.7.8.0", {"start": v(28.13, -31.75) * mm, "end": v(28.13, -25.4) * mm});
            skLineSegment(sketch, "E92.13.8.0", {"start": v(28.13, -20.32) * mm, "end": v(28.13, -10.16) * mm});
            skArc(sketch, "E92.16.8.0", {"start": v(28.13, 5.08) * mm, "mid": v(29.08, 6.03) * mm, "end": v(30.04, 5.08) * mm});
            skLineSegment(sketch, "E92.20.8.0", {"start": v(29.08, 5.08) * mm, "end": v(29.08, 0) * mm});
            skLineSegment(sketch, "E92.35.8.0", {"start": v(29.08, -10.16) * mm, "end": v(29.08, -5.08) * mm, "construction": true});
            skLineSegment(sketch, "E92.38.8.0", {"start": v(29.08, -5.08) * mm, "end": v(29.08, 0) * mm});
            skLineSegment(sketch, "E92.44.8.0", {"start": v(30.04, 5.08) * mm, "end": v(30.04, 0) * mm});
            skLineSegment(sketch, "E92.47.8.0", {"start": v(28.13, 5.08) * mm, "end": v(28.13, 0) * mm});
            skLineSegment(sketch, "E92.53.8.0", {"start": v(30.04, -20.32) * mm, "end": v(30.04, -10.16) * mm});
            skLineSegment(sketch, "E92.56.8.0", {"start": v(30.04, 31.75) * mm, "end": v(30.04, 25.4) * mm});
            skLineSegment(sketch, "E92.62.8.0", {"start": v(29.08, -25.4) * mm, "end": v(29.08, -20.32) * mm, "construction": true});
            skLineSegment(sketch, "E92.68.8.0", {"start": v(30.04, -5.08) * mm, "end": v(30.04, 0) * mm});
            skLineSegment(sketch, "E92.71.8.0", {"start": v(29.08, -31.75) * mm, "end": v(29.08, -25.4) * mm});
            skLineSegment(sketch, "E92.80.8.0", {"start": v(29.08, 20.32) * mm, "end": v(29.08, 10.16) * mm});
            skLineSegment(sketch, "E92.86.8.0", {"start": v(29.08, -20.32) * mm, "end": v(29.08, -10.16) * mm});
            skLineSegment(sketch, "E92.89.8.0", {"start": v(30.04, 20.32) * mm, "end": v(30.04, 10.16) * mm});
            skLineSegment(sketch, "E92.92.8.0", {"start": v(29.08, 25.4) * mm, "end": v(29.08, 20.32) * mm, "construction": true});
            skLineSegment(sketch, "E92.95.8.0", {"start": v(29.08, 10.16) * mm, "end": v(29.08, 5.08) * mm, "construction": true});
            skLineSegment(sketch, "E92.98.8.0", {"start": v(30.04, -31.75) * mm, "end": v(30.04, -25.4) * mm});
            skLineSegment(sketch, "E92.101.8.0", {"start": v(28.13, -5.08) * mm, "end": v(28.13, 0) * mm});
            skLineSegment(sketch, "E92.104.8.0", {"start": v(28.13, 20.32) * mm, "end": v(28.13, 10.16) * mm});
            skLineSegment(sketch, "E92.110.8.0", {"start": v(29.08, 31.75) * mm, "end": v(29.08, 25.4) * mm});
            skLineSegment(sketch, "E92.113.8.0", {"start": v(28.13, 31.75) * mm, "end": v(28.13, 25.4) * mm});
            skArc(sketch, "E92.122.8.0", {"start": v(28.13, -5.08) * mm, "mid": v(29.08, -6.03) * mm, "end": v(30.04, -5.08) * mm});
            skArc(sketch, "E92.129.8.0", {"start": v(30.04, 25.4) * mm, "mid": v(29.08, 24.45) * mm, "end": v(28.13, 25.4) * mm});
            skArc(sketch, "E92.144.8.0", {"start": v(28.13, -20.32) * mm, "mid": v(29.08, -21.27) * mm, "end": v(30.04, -20.32) * mm});
            skArc(sketch, "E92.152.8.0", {"start": v(30.04, 10.16) * mm, "mid": v(29.08, 9.2) * mm, "end": v(28.13, 10.16) * mm});
            skArc(sketch, "E92.156.8.0", {"start": v(28.13, 20.32) * mm, "mid": v(29.08, 21.27) * mm, "end": v(30.04, 20.32) * mm});
            skArc(sketch, "E92.164.8.0", {"start": v(30.04, -10.16) * mm, "mid": v(29.08, -9.2) * mm, "end": v(28.13, -10.16) * mm});
            skLineSegment(sketch, "E92.168.8.0", {"start": v(30.04, -31.75) * mm, "end": v(28.13, -31.75) * mm});
            skLineSegment(sketch, "E92.175.8.0", {"start": v(30.04, 31.75) * mm, "end": v(28.13, 31.75) * mm});
            skSolve(sketch);
        }
        {
            var Q0;
            Q0 = qSketchRegion(id + "F4", true);
            extrude(context, id + "F5", {"entities" : qUnion([Q0]), "operationType" : NewBodyOperationType.REMOVE, "oppositeDirection" : true, "depth" : 25.4 * mm, "offsetDistance" : 25.4 * mm});
        }
    });
